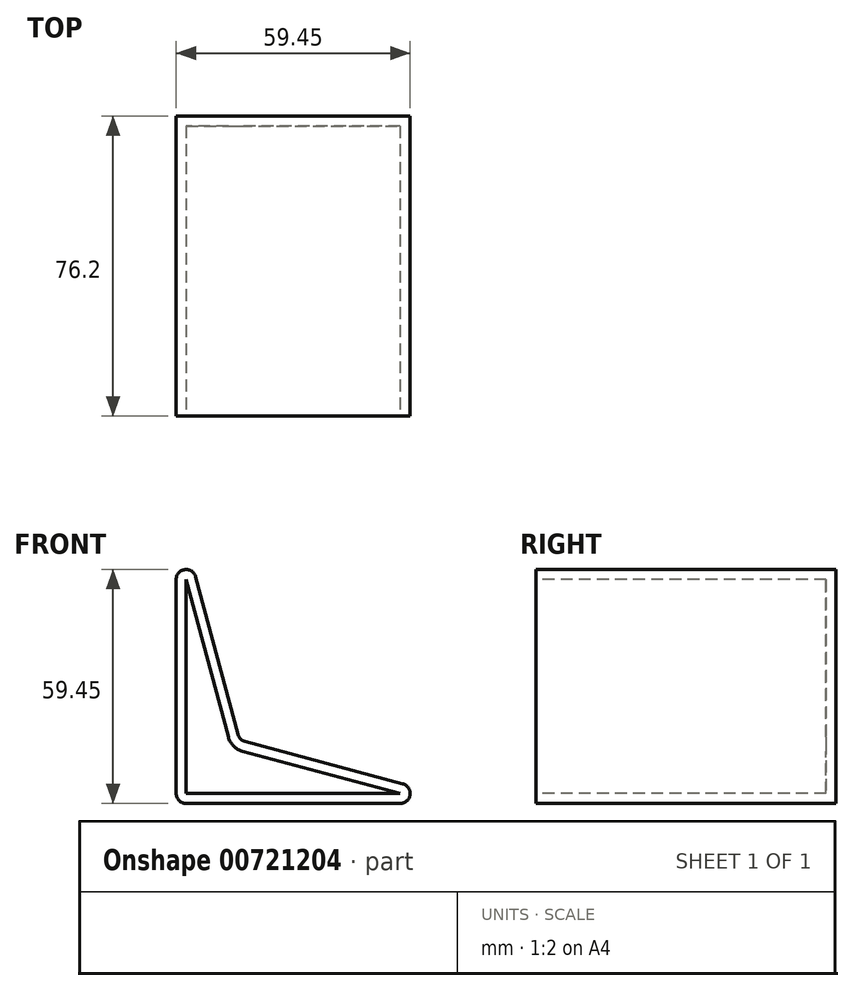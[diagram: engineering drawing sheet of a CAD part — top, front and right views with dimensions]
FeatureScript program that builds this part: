
annotation { "Feature Type Name" : "Feature", "Feature Type Description" : "" }
export const myFeature = defineFeature(function(context is Context, id is Id, definition is map)
    precondition{}
    {
        {
            var Q0;
            Q0=qCreatedBy(makeId("Front.planeOp"),FACE);
            var sketch = newSketch(context, id + "F0", { "sketchPlane" : qUnion([Q0])});
            skLineSegment(sketch, "E0", {"start": v(0, 76.2) * mm, "end": v(0, 0) * mm});
            skLineSegment(sketch, "E1", {"start": v(0, 0) * mm, "end": v(76.2, 0) * mm});
            skLineSegment(sketch, "E2", {"start": v(76.2, 0) * mm, "end": v(16.1, 16.1) * mm});
            skLineSegment(sketch, "E3", {"start": v(16.1, 16.1) * mm, "end": v(0, 76.2) * mm});
            skSolve(sketch);
        }
        {
            var Q0;
            Q0 = qSketchRegion(id + "F0", true);
            extrude(context, id + "F1", {"entities" : qUnion([Q0]), "depth" : 76.2 * mm, "offsetDistance" : 25.4 * mm});
        }
        {
            var Q0;
            Q0=makeQuery(id+"F1.opExtrude","SWEPT_EDGE",EDGE,{"disambiguationData":[OSD([sQuery(id+"F0.wireOp",EDGE,"E0"),sQuery(id+"F0.wireOp",EDGE,"E3")])]});
            var Q1;
            Q1=makeQuery(id+"F1.opExtrude","SWEPT_EDGE",EDGE,{"disambiguationData":[OSD([sQuery(id+"F0.wireOp",EDGE,"E1"),sQuery(id+"F0.wireOp",EDGE,"E2")])]});
            var Q2;
            Q2=makeQuery(id+"F1.opExtrude","SWEPT_EDGE",EDGE,{"disambiguationData":[OSD([sQuery(id+"F0.wireOp",EDGE,"E2"),sQuery(id+"F0.wireOp",EDGE,"E3")])]});
            var Q3;
            Q3=makeQuery(id+"F1.opExtrude","SWEPT_EDGE",EDGE,{"disambiguationData":[OSD([sQuery(id+"F0.wireOp",EDGE,"E0"),sQuery(id+"F0.wireOp",EDGE,"E1")])]});
            fillet(context, id + "F2", {"entities" : qUnion([Q0, Q1, Q2, Q3]), "radius" : 2.54 * mm, "tangentPropagation" : true, "allowEdgeOverflow" : false});
        }
        {
            var Q0;
            Q0=makeQuery(id+"F1.opExtrude","CAP_FACE",FACE,{"disambiguationData":[OSD([sQuery(id+"F0.wireOp",EDGE,"E0"),sQuery(id+"F0.wireOp",EDGE,"E1"),sQuery(id+"F0.wireOp",EDGE,"E2"),sQuery(id+"F0.wireOp",EDGE,"E3")])],"isStart":false});
            shell(context, id + "F3", {"entities" : qUnion([Q0]), "thickness" : 2.54 * mm});
        }
    });
